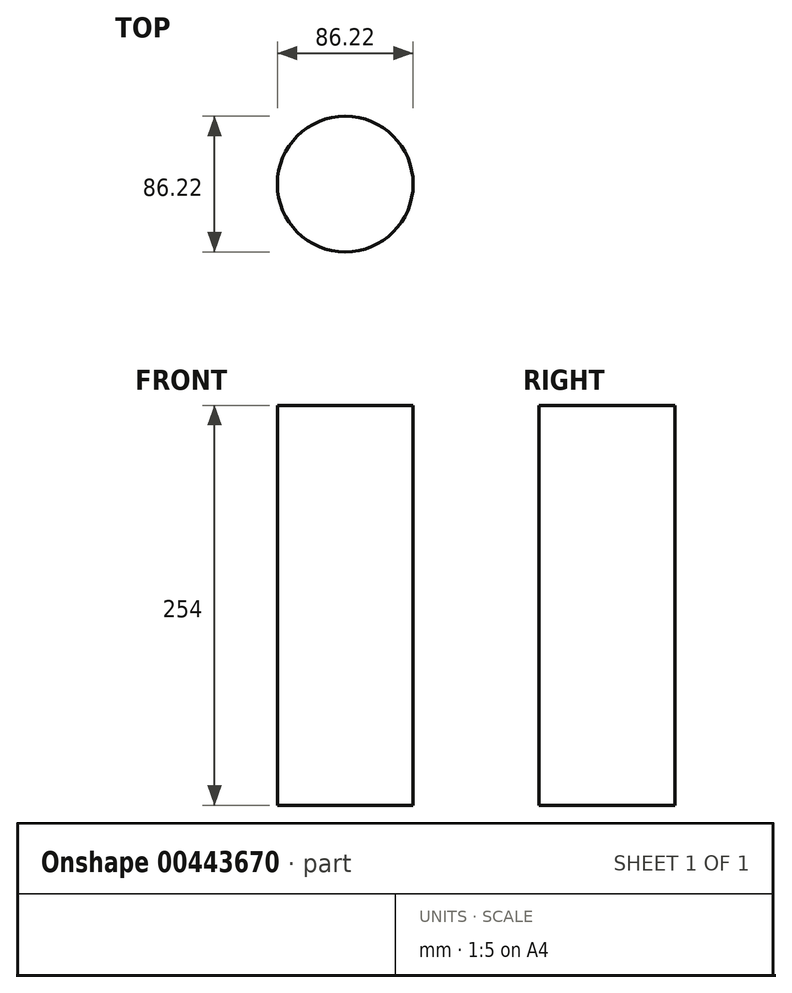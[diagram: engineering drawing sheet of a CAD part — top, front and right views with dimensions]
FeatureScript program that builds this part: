
annotation { "Feature Type Name" : "Feature", "Feature Type Description" : "" }
export const myFeature = defineFeature(function(context is Context, id is Id, definition is map)
    precondition{}
    {
        {
            var Q0;
            Q0=qCreatedBy(makeId("Top.planeOp"),FACE);
            var sketch = newSketch(context, id + "F0", { "sketchPlane" : qUnion([Q0])});
            skCircle(sketch, "E0", {"center": v(0, 0) * mm, "radius": 43.1 * mm});
            skSolve(sketch);
        }
        {
            var Q0;
            Q0=makeQuery(id+"F0.imprint","IMPRINT",FACE,{"disambiguationData":[TD([[makeQuery(id+"F0.imprint","IMPRINT",EDGE,{"derivedFrom":sQuery(id+"F0.wireOp",EDGE,"E0")}),1.0]])]});
            extrude(context, id + "F1", {"entities" : qUnion([Q0]), "depth" : 254 * mm});
        }
    });
